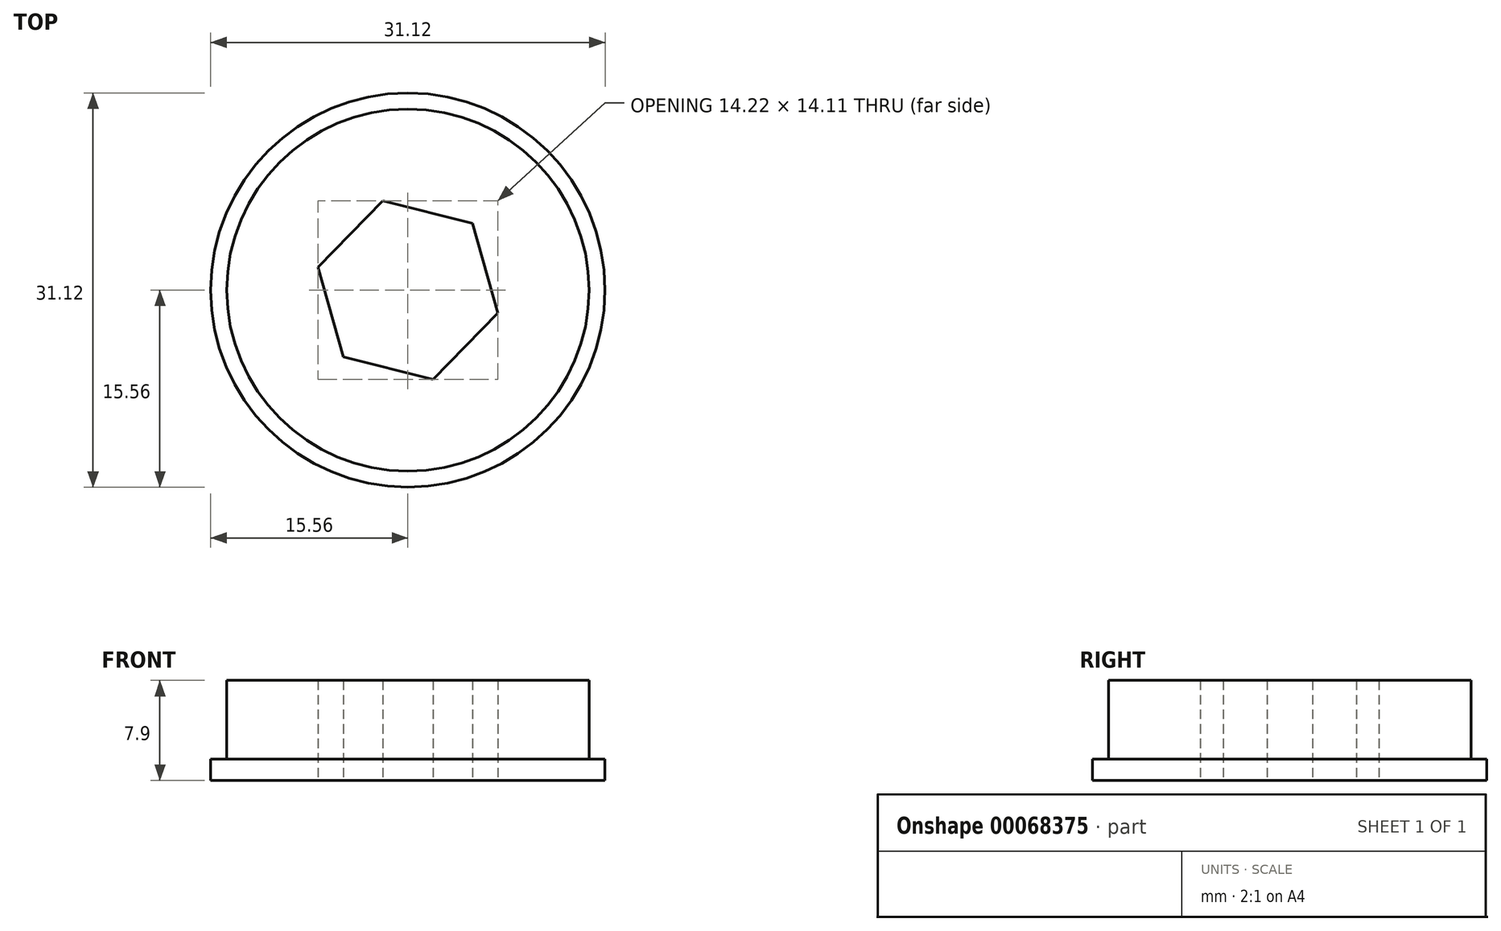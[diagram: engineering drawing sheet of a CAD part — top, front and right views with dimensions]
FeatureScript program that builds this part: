
annotation { "Feature Type Name" : "Feature", "Feature Type Description" : "" }
export const myFeature = defineFeature(function(context is Context, id is Id, definition is map)
    precondition{}
    {
        {
            var Q0;
            Q0=qCreatedBy(makeId("Top.planeOp"),FACE);
            var sketch = newSketch(context, id + "F0", { "sketchPlane" : qUnion([Q0])});
            skCircle(sketch, "E0.cCircle", {"center": v(0, 0) * mm, "radius": 6.35 * mm, "construction": true});
            skLineSegment(sketch, "E0.0", {"start": v(7.1, -1.8) * mm, "end": v(2, -7.05) * mm});
            skLineSegment(sketch, "E0.1", {"start": v(2, -7.05) * mm, "end": v(-5.1, -5.26) * mm});
            skLineSegment(sketch, "E0.2", {"start": v(-5.1, -5.26) * mm, "end": v(-7.1, 1.8) * mm});
            skLineSegment(sketch, "E0.3", {"start": v(-7.1, 1.8) * mm, "end": v(-2, 7.05) * mm});
            skLineSegment(sketch, "E0.4", {"start": v(-2, 7.05) * mm, "end": v(5.1, 5.26) * mm});
            skLineSegment(sketch, "E0.5", {"start": v(5.1, 5.26) * mm, "end": v(7.1, -1.8) * mm});
            skPoint(sketch, "E0.0.midPoint", {"position": v(4.55, -4.43) * mm});
            skSolve(sketch);
        }
        {
            var Q0;
            Q0=qCreatedBy(makeId("Top.planeOp"),FACE);
            var sketch = newSketch(context, id + "F1", { "sketchPlane" : qUnion([Q0])});
            skCircle(sketch, "E1", {"center": v(0, 0) * mm, "radius": 14.3 * mm});
            skSolve(sketch);
        }
        {
            var Q0;
            Q0=qCreatedBy(makeId("Top.planeOp"),FACE);
            var sketch = newSketch(context, id + "F2", { "sketchPlane" : qUnion([Q0])});
            skCircle(sketch, "E2", {"center": v(0, 0) * mm, "radius": 15.56 * mm});
            skSolve(sketch);
        }
        {
            var Q0;
            Q0 = qSketchRegion(id + "F2", true);
            extrude(context, id + "F3", {"entities" : qUnion([Q0]), "depth" : 1.69 * mm});
        }
        {
            var Q0;
            Q0 = qSketchRegion(id + "F1", true);
            extrude(context, id + "F4", {"entities" : qUnion([Q0]), "operationType" : NewBodyOperationType.ADD, "depth" : 7.9 * mm});
        }
        {
            var Q0;
            Q0 = qSketchRegion(id + "F0", true);
            extrude(context, id + "F5", {"entities" : qUnion([Q0]), "operationType" : NewBodyOperationType.REMOVE, "depth" : 25.4 * mm});
        }
    });
